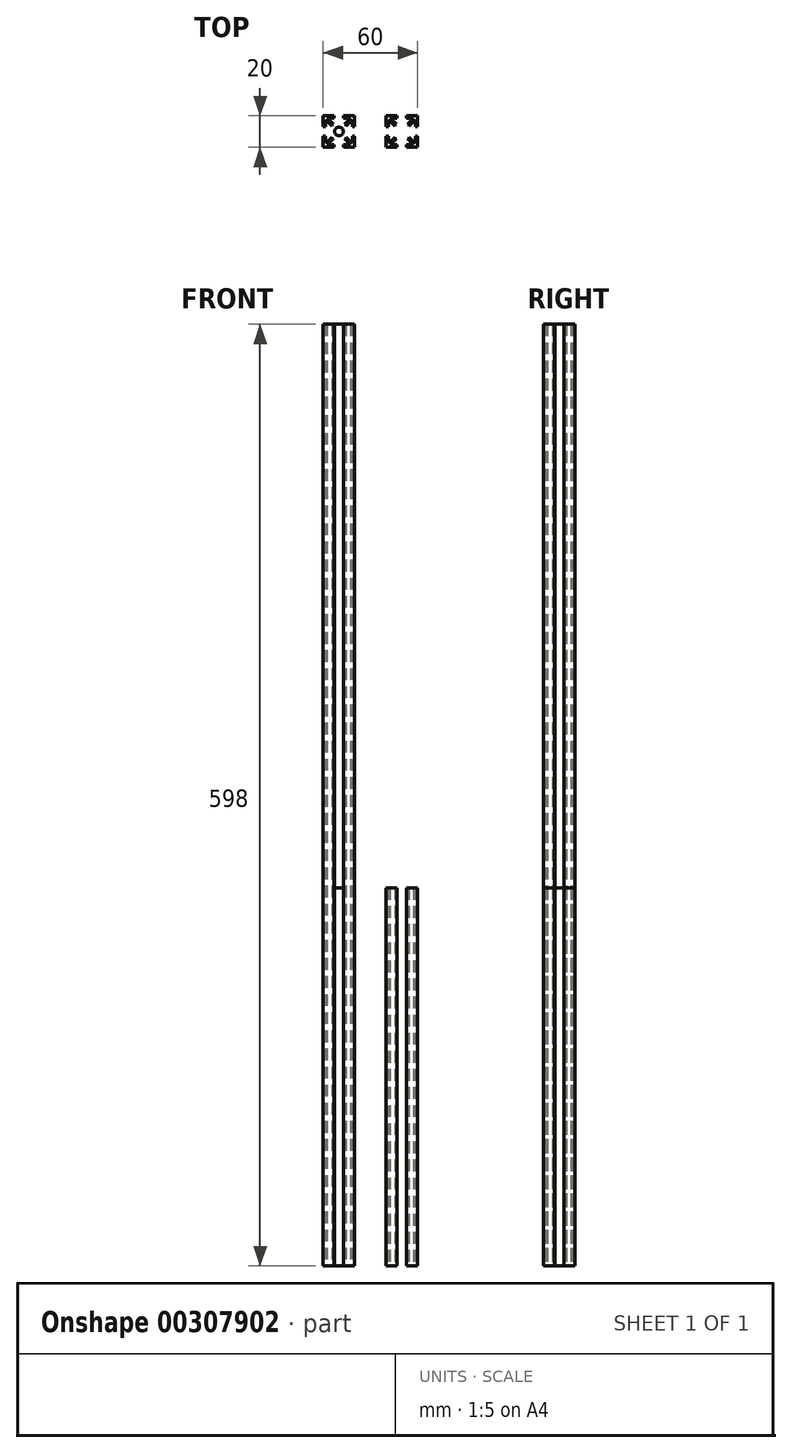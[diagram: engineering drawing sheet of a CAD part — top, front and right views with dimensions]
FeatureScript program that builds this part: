
annotation { "Feature Type Name" : "Feature", "Feature Type Description" : "" }
export const myFeature = defineFeature(function(context is Context, id is Id, definition is map)
    precondition{}
    {
        {
            var Q0;
            Q0=qCreatedBy(makeId("Top.planeOp"),FACE);
            var sketch = newSketch(context, id + "F0", { "sketchPlane" : qUnion([Q0])});
            skLineSegment(sketch, "E0", {"start": v(0, 10) * mm, "end": v(10, 10) * mm, "construction": true});
            skLineSegment(sketch, "E1", {"start": v(10, 10) * mm, "end": v(10, 0) * mm, "construction": true});
            skLineSegment(sketch, "E2", {"start": v(10, 10) * mm, "end": v(0, 0) * mm, "construction": true});
            skArc(sketch, "E3", {"start": v(0, 2.75) * mm, "mid": v(1.94, 1.94) * mm, "end": v(2.75, 0) * mm});
            skLineSegment(sketch, "E4", {"start": v(4.5, 0) * mm, "end": v(4.5, 4.5) * mm});
            skLineSegment(sketch, "E5", {"start": v(4.5, 4.5) * mm, "end": v(0, 4.5) * mm});
            skLineSegment(sketch, "E6", {"start": v(3.47, 4.5) * mm, "end": v(7.47, 8.5) * mm});
            skLineSegment(sketch, "E7", {"start": v(7.47, 8.5) * mm, "end": v(3, 8.5) * mm});
            skLineSegment(sketch, "E8", {"start": v(3, 8.5) * mm, "end": v(3, 10) * mm});
            skLineSegment(sketch, "E9", {"start": v(3, 10) * mm, "end": v(10, 10) * mm});
            skLineSegment(sketch, "E10", {"start": v(10, 3) * mm, "end": v(8.5, 3) * mm});
            skLineSegment(sketch, "E11", {"start": v(8.5, 3) * mm, "end": v(8.5, 7.47) * mm});
            skLineSegment(sketch, "E12", {"start": v(8.5, 7.47) * mm, "end": v(4.5, 3.47) * mm});
            skLineSegment(sketch, "E13", {"start": v(10, 3) * mm, "end": v(10, 10) * mm});
            skLineSegment(sketch, "E14.1.0", {"start": v(-3, 10) * mm, "end": v(-3, 8.5) * mm});
            skLineSegment(sketch, "E14.1.1", {"start": v(0, 4.5) * mm, "end": v(-4.5, 4.5) * mm});
            skLineSegment(sketch, "E14.1.2", {"start": v(-4.5, 3.47) * mm, "end": v(-8.5, 7.47) * mm});
            skLineSegment(sketch, "E14.1.3", {"start": v(-10, 0) * mm, "end": v(-10, 10) * mm, "construction": true});
            skArc(sketch, "E14.1.4", {"start": v(-2.75, 0) * mm, "mid": v(-1.94, 1.94) * mm, "end": v(0, 2.75) * mm});
            skLineSegment(sketch, "E14.1.5", {"start": v(-8.5, 3) * mm, "end": v(-10, 3) * mm});
            skLineSegment(sketch, "E14.1.6", {"start": v(-10, 3) * mm, "end": v(-10, 10) * mm});
            skLineSegment(sketch, "E14.1.7", {"start": v(-7.47, 8.5) * mm, "end": v(-3.47, 4.5) * mm});
            skLineSegment(sketch, "E14.1.8", {"start": v(-3, 8.5) * mm, "end": v(-7.47, 8.5) * mm});
            skLineSegment(sketch, "E14.1.9", {"start": v(-4.5, 4.5) * mm, "end": v(-4.5, 0) * mm});
            skLineSegment(sketch, "E14.1.10", {"start": v(-10, 10) * mm, "end": v(0, 10) * mm, "construction": true});
            skLineSegment(sketch, "E14.1.11", {"start": v(-10, 10) * mm, "end": v(0, 0) * mm, "construction": true});
            skLineSegment(sketch, "E14.1.12", {"start": v(-8.5, 7.47) * mm, "end": v(-8.5, 3) * mm});
            skLineSegment(sketch, "E14.1.13", {"start": v(-3, 10) * mm, "end": v(-10, 10) * mm});
            skLineSegment(sketch, "E14.2.0", {"start": v(-10, -3) * mm, "end": v(-8.5, -3) * mm});
            skLineSegment(sketch, "E14.2.1", {"start": v(-4.5, 0) * mm, "end": v(-4.5, -4.5) * mm});
            skLineSegment(sketch, "E14.2.2", {"start": v(-3.47, -4.5) * mm, "end": v(-7.47, -8.5) * mm});
            skLineSegment(sketch, "E14.2.3", {"start": v(0, -10) * mm, "end": v(-10, -10) * mm, "construction": true});
            skArc(sketch, "E14.2.4", {"start": v(0, -2.75) * mm, "mid": v(-1.94, -1.94) * mm, "end": v(-2.75, 0) * mm});
            skLineSegment(sketch, "E14.2.5", {"start": v(-3, -8.5) * mm, "end": v(-3, -10) * mm});
            skLineSegment(sketch, "E14.2.6", {"start": v(-3, -10) * mm, "end": v(-10, -10) * mm});
            skLineSegment(sketch, "E14.2.7", {"start": v(-8.5, -7.47) * mm, "end": v(-4.5, -3.47) * mm});
            skLineSegment(sketch, "E14.2.8", {"start": v(-8.5, -3) * mm, "end": v(-8.5, -7.47) * mm});
            skLineSegment(sketch, "E14.2.9", {"start": v(-4.5, -4.5) * mm, "end": v(0, -4.5) * mm});
            skLineSegment(sketch, "E14.2.10", {"start": v(-10, -10) * mm, "end": v(-10, 0) * mm, "construction": true});
            skLineSegment(sketch, "E14.2.11", {"start": v(-10, -10) * mm, "end": v(0, 0) * mm, "construction": true});
            skLineSegment(sketch, "E14.2.12", {"start": v(-7.47, -8.5) * mm, "end": v(-3, -8.5) * mm});
            skLineSegment(sketch, "E14.2.13", {"start": v(-10, -3) * mm, "end": v(-10, -10) * mm});
            skLineSegment(sketch, "E14.3.0", {"start": v(3, -10) * mm, "end": v(3, -8.5) * mm});
            skLineSegment(sketch, "E14.3.1", {"start": v(0, -4.5) * mm, "end": v(4.5, -4.5) * mm});
            skLineSegment(sketch, "E14.3.2", {"start": v(4.5, -3.47) * mm, "end": v(8.5, -7.47) * mm});
            skLineSegment(sketch, "E14.3.3", {"start": v(10, 0) * mm, "end": v(10, -10) * mm, "construction": true});
            skArc(sketch, "E14.3.4", {"start": v(2.75, 0) * mm, "mid": v(1.94, -1.94) * mm, "end": v(0, -2.75) * mm});
            skLineSegment(sketch, "E14.3.5", {"start": v(8.5, -3) * mm, "end": v(10, -3) * mm});
            skLineSegment(sketch, "E14.3.6", {"start": v(10, -3) * mm, "end": v(10, -10) * mm});
            skLineSegment(sketch, "E14.3.7", {"start": v(7.47, -8.5) * mm, "end": v(3.47, -4.5) * mm});
            skLineSegment(sketch, "E14.3.8", {"start": v(3, -8.5) * mm, "end": v(7.47, -8.5) * mm});
            skLineSegment(sketch, "E14.3.9", {"start": v(4.5, -4.5) * mm, "end": v(4.5, 0) * mm});
            skLineSegment(sketch, "E14.3.10", {"start": v(10, -10) * mm, "end": v(0, -10) * mm, "construction": true});
            skLineSegment(sketch, "E14.3.11", {"start": v(10, -10) * mm, "end": v(0, 0) * mm, "construction": true});
            skLineSegment(sketch, "E14.3.12", {"start": v(8.5, -7.47) * mm, "end": v(8.5, -3) * mm});
            skLineSegment(sketch, "E14.3.13", {"start": v(3, -10) * mm, "end": v(10, -10) * mm});
            skSolve(sketch);
        }
        {
            var Q0;
            Q0=makeQuery(id+"F0.imprint","IMPRINT",FACE,{"disambiguationData":[TD([[makeQuery(id+"F0.imprint","IMPRINT",EDGE,{"derivedFrom":sQuery(id+"F0.wireOp",EDGE,"E14.1.0")}),-1.0]])]});
            var Q1;
            {var subQ0=sQuery(id+"F0.wireOp",EDGE,"E6");Q1=makeQuery(id+"F0.imprint","IMPRINT",FACE,{"disambiguationData":[TD([[makeQuery(id+"F0.imprint","IMPRINT",EDGE,{"derivedFrom":subQ0}),-1.0]])]});}
            var Q2;
            Q2=makeQuery(id+"F0.imprint","IMPRINT",FACE,{"disambiguationData":[TD([[makeQuery(id+"F0.imprint","IMPRINT",EDGE,{"derivedFrom":sQuery(id+"F0.wireOp",EDGE,"E3")}),1.0]])]});
            var Q3;
            Q3=makeQuery(id+"F0.imprint","IMPRINT",FACE,{"disambiguationData":[TD([[makeQuery(id+"F0.imprint","IMPRINT",EDGE,{"derivedFrom":sQuery(id+"F0.wireOp",EDGE,"E14.3.0")}),-1.0]])]});
            var Q4;
            Q4=makeQuery(id+"F0.imprint","IMPRINT",FACE,{"disambiguationData":[TD([[makeQuery(id+"F0.imprint","IMPRINT",EDGE,{"derivedFrom":sQuery(id+"F0.wireOp",EDGE,"E14.2.0")}),-1.0]])]});
            extrude(context, id + "F1", {"entities" : qUnion([Q0, Q1, Q2, Q3, Q4]), "depth" : 598 * mm});
        }
        {
            var Q0;
            Q0=makeQuery(id+"F0.imprint","IMPRINT",FACE,{"disambiguationData":[TD([[makeQuery(id+"F0.imprint","IMPRINT",EDGE,{"derivedFrom":sQuery(id+"F0.wireOp",EDGE,"E14.1.0")}),-1.0]])]});
            var Q1;
            Q1=makeQuery(id+"F0.imprint","IMPRINT",FACE,{"disambiguationData":[TD([[makeQuery(id+"F0.imprint","IMPRINT",EDGE,{"derivedFrom":sQuery(id+"F0.wireOp",EDGE,"E3")}),1.0]])]});
            var Q2;
            {var subQ0=sQuery(id+"F0.wireOp",EDGE,"E6");Q2=makeQuery(id+"F0.imprint","IMPRINT",FACE,{"disambiguationData":[TD([[makeQuery(id+"F0.imprint","IMPRINT",EDGE,{"derivedFrom":subQ0}),-1.0]])]});}
            var Q3;
            Q3=makeQuery(id+"F0.imprint","IMPRINT",FACE,{"disambiguationData":[TD([[makeQuery(id+"F0.imprint","IMPRINT",EDGE,{"derivedFrom":sQuery(id+"F0.wireOp",EDGE,"E14.3.0")}),-1.0]])]});
            var Q4;
            Q4=makeQuery(id+"F0.imprint","IMPRINT",FACE,{"disambiguationData":[TD([[makeQuery(id+"F0.imprint","IMPRINT",EDGE,{"derivedFrom":sQuery(id+"F0.wireOp",EDGE,"E14.2.0")}),-1.0]])]});
            extrude(context, id + "F2", {"entities" : qUnion([Q0, Q1, Q2, Q3, Q4]), "depth" : 240 * mm});
        }
        {
            var Q0;
            Q0=makeQuery(id+"F2.opExtrude","SWEPT_BODY",BODY,{"disambiguationData":[OSD([sQuery(id+"F0.wireOp",EDGE,"E3"),sQuery(id+"F0.wireOp",EDGE,"E4"),sQuery(id+"F0.wireOp",EDGE,"E5"),sQuery(id+"F0.wireOp",EDGE,"E6"),sQuery(id+"F0.wireOp",EDGE,"E7"),sQuery(id+"F0.wireOp",EDGE,"E8"),sQuery(id+"F0.wireOp",EDGE,"E9"),sQuery(id+"F0.wireOp",EDGE,"E10"),sQuery(id+"F0.wireOp",EDGE,"E11"),sQuery(id+"F0.wireOp",EDGE,"E12"),sQuery(id+"F0.wireOp",EDGE,"E13"),sQuery(id+"F0.wireOp",EDGE,"E14.1.0"),sQuery(id+"F0.wireOp",EDGE,"E14.1.1"),sQuery(id+"F0.wireOp",EDGE,"E14.1.2"),sQuery(id+"F0.wireOp",EDGE,"E14.1.4"),sQuery(id+"F0.wireOp",EDGE,"E14.1.5"),sQuery(id+"F0.wireOp",EDGE,"E14.1.6"),sQuery(id+"F0.wireOp",EDGE,"E14.1.7"),sQuery(id+"F0.wireOp",EDGE,"E14.1.8"),sQuery(id+"F0.wireOp",EDGE,"E14.1.9"),sQuery(id+"F0.wireOp",EDGE,"E14.1.12"),sQuery(id+"F0.wireOp",EDGE,"E14.1.13"),sQuery(id+"F0.wireOp",EDGE,"E14.2.0"),sQuery(id+"F0.wireOp",EDGE,"E14.2.1"),sQuery(id+"F0.wireOp",EDGE,"E14.2.2"),sQuery(id+"F0.wireOp",EDGE,"E14.2.4"),sQuery(id+"F0.wireOp",EDGE,"E14.2.5"),sQuery(id+"F0.wireOp",EDGE,"E14.2.6"),sQuery(id+"F0.wireOp",EDGE,"E14.2.7"),sQuery(id+"F0.wireOp",EDGE,"E14.2.8"),sQuery(id+"F0.wireOp",EDGE,"E14.2.9"),sQuery(id+"F0.wireOp",EDGE,"E14.2.12"),sQuery(id+"F0.wireOp",EDGE,"E14.2.13"),sQuery(id+"F0.wireOp",EDGE,"E14.3.0"),sQuery(id+"F0.wireOp",EDGE,"E14.3.1"),sQuery(id+"F0.wireOp",EDGE,"E14.3.2"),sQuery(id+"F0.wireOp",EDGE,"E14.3.4"),sQuery(id+"F0.wireOp",EDGE,"E14.3.5"),sQuery(id+"F0.wireOp",EDGE,"E14.3.6"),sQuery(id+"F0.wireOp",EDGE,"E14.3.7"),sQuery(id+"F0.wireOp",EDGE,"E14.3.8"),sQuery(id+"F0.wireOp",EDGE,"E14.3.9"),sQuery(id+"F0.wireOp",EDGE,"E14.3.12"),sQuery(id+"F0.wireOp",EDGE,"E14.3.13")])]});
            transform(context, id + "F3", {"entities" : qUnion([Q0]), "transformType" : TransformType.TRANSLATION_3D, "dx" : 40 * mm, "dy" : 0 * mm, "dz" : 0 * mm, "makeCopy" : false});
        }
    });
